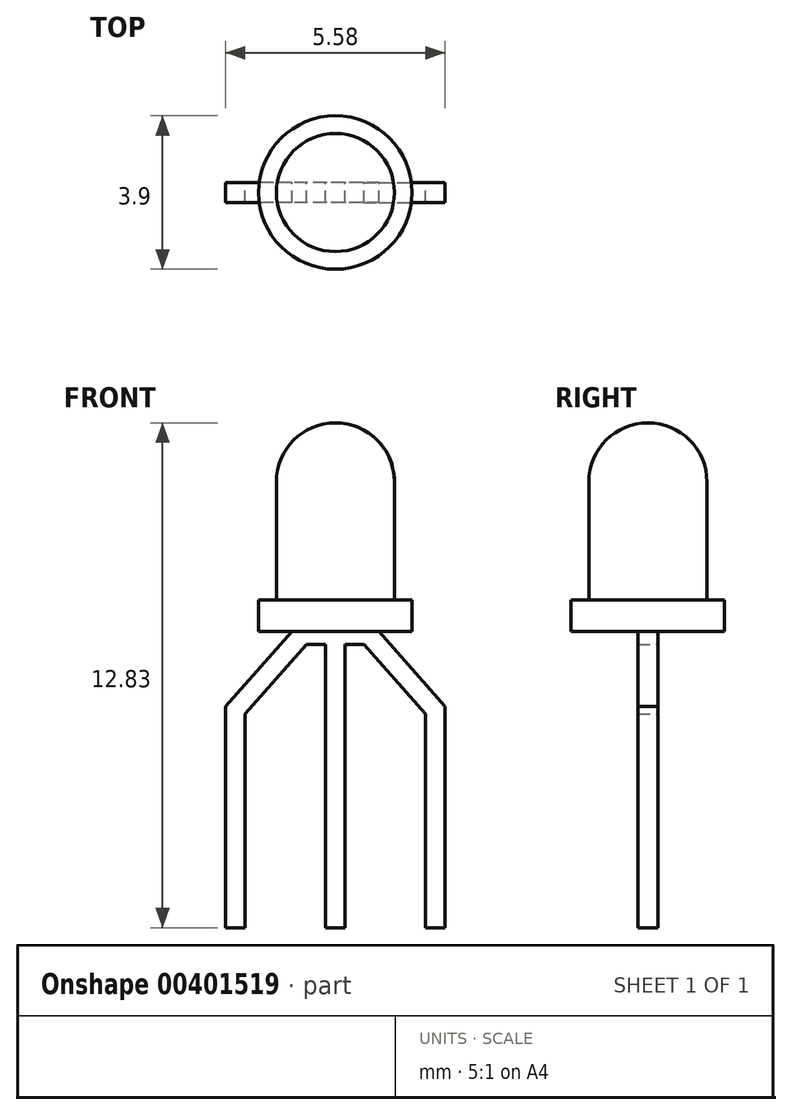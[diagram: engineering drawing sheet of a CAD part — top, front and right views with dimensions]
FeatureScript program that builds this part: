
annotation { "Feature Type Name" : "Feature", "Feature Type Description" : "" }
export const myFeature = defineFeature(function(context is Context, id is Id, definition is map)
    precondition{}
    {
        {
            var Q0;
            Q0=qCreatedBy(makeId("Top.planeOp"),FACE);
            var sketch = newSketch(context, id + "F0", { "sketchPlane" : qUnion([Q0])});
            skCircle(sketch, "E0", {"center": v(0, 0) * mm, "radius": 1.95 * mm});
            skSolve(sketch);
        }
        {
            var Q0;
            Q0=qSketchRegion(id+"F0",true);
            extrude(context, id + "F1", {"entities" : qUnion([Q0]), "depth" : .8 * mm});
        }
        {
            var Q0;
            Q0=makeQuery(id+"F1.opExtrude","CAP_FACE",FACE,{"disambiguationData":[OSD([sQuery(id+"F0.wireOp",EDGE,"E0")])],"isStart":false});
            var sketch = newSketch(context, id + "F2", { "sketchPlane" : qUnion([Q0])});
            skCircle(sketch, "E1", {"center": v(0, 0) * mm, "radius": 1.5 * mm});
            skSolve(sketch);
        }
        {
            var Q0;
            Q0=qSketchRegion(id+"F2",true);
            extrude(context, id + "F3", {"entities" : qUnion([Q0]), "operationType" : NewBodyOperationType.ADD, "depth" : 4.5 * mm});
        }
        {
            var Q0;
            Q0=makeQuery(id+"F3.opExtrude","CAP_EDGE",EDGE,{"disambiguationData":[OSD([sQuery(id+"F2.wireOp",EDGE,"E1")])],"isStart":false});
            fillet(context, id + "F4", {"entities" : qUnion([Q0]), "radius" : 1.5 * mm, "tangentPropagation" : true, "allowEdgeOverflow" : false});
        }
        {
            var Q0;
            Q0=qCreatedBy(makeId("Front.planeOp"),FACE);
            var sketch = newSketch(context, id + "F5", { "sketchPlane" : qUnion([Q0])});
            skLineSegment(sketch, "E2", {"start": v(0, -0.9) * mm, "end": v(0, -7.84) * mm});
            skLineSegment(sketch, "E3", {"start": v(-2.54, -0.9) * mm, "end": v(-2.54, -7.96) * mm});
            skLineSegment(sketch, "E4", {"start": v(2.54, -0.97) * mm, "end": v(2.54, -7.53) * mm});
            skLineSegment(sketch, "E5.0", {"start": v(2.29, -0.97) * mm, "end": v(2.3, -7.53) * mm});
            skLineSegment(sketch, "E6.0", {"start": v(2.8, -0.97) * mm, "end": v(2.8, -7.53) * mm});
            skLineSegment(sketch, "E7.0", {"start": v(-0.25, -0.33) * mm, "end": v(-0.25, -7.84) * mm});
            skLineSegment(sketch, "E8.0", {"start": v(0.25, -0.33) * mm, "end": v(0.25, -7.84) * mm});
            skLineSegment(sketch, "E9.0", {"start": v(-2.3, -0.9) * mm, "end": v(-2.3, -7.96) * mm});
            skLineSegment(sketch, "E10.0", {"start": v(-2.8, -0.9) * mm, "end": v(-2.79, -7.96) * mm});
            skLineSegment(sketch, "E11", {"start": v(1.1, 0) * mm, "end": v(2.8, -1.9) * mm});
            skLineSegment(sketch, "E12.MirrorCS", {"start": v(-1.1, 0) * mm, "end": v(-2.8, -1.9) * mm});
            skLineSegment(sketch, "E13.0", {"start": v(0.73, -0.33) * mm, "end": v(2.42, -2.24) * mm});
            skLineSegment(sketch, "E14.0", {"start": v(-0.73, -0.33) * mm, "end": v(-2.42, -2.24) * mm});
            skLineSegment(sketch, "E15", {"start": v(0.73, -0.33) * mm, "end": v(-0.73, -0.33) * mm});
            skLineSegment(sketch, "E16", {"start": v(1.1, 0) * mm, "end": v(-1.1, 0) * mm});
            skLineSegment(sketch, "E17", {"start": v(2.8, -7.53) * mm, "end": v(2.3, -7.53) * mm});
            skLineSegment(sketch, "E18.trimOffspring", {"start": v(-2.3, -7.53) * mm, "end": v(-2.8, -7.53) * mm});
            skLineSegment(sketch, "E19.trimOffspring", {"start": v(0.25, -7.53) * mm, "end": v(-0.25, -7.53) * mm});
            skSolve(sketch);
        }
        {
            var Q0;
            Q0=qSketchRegion(id+"F5",true);
            extrude(context, id + "F6", {"entities" : qUnion([Q0]), "operationType" : NewBodyOperationType.ADD, "depth" : .25 * mm, "hasSecondDirection" : true, "secondDirectionOppositeDirection" : true, "secondDirectionDepth" : .25 * mm});
        }
    });
